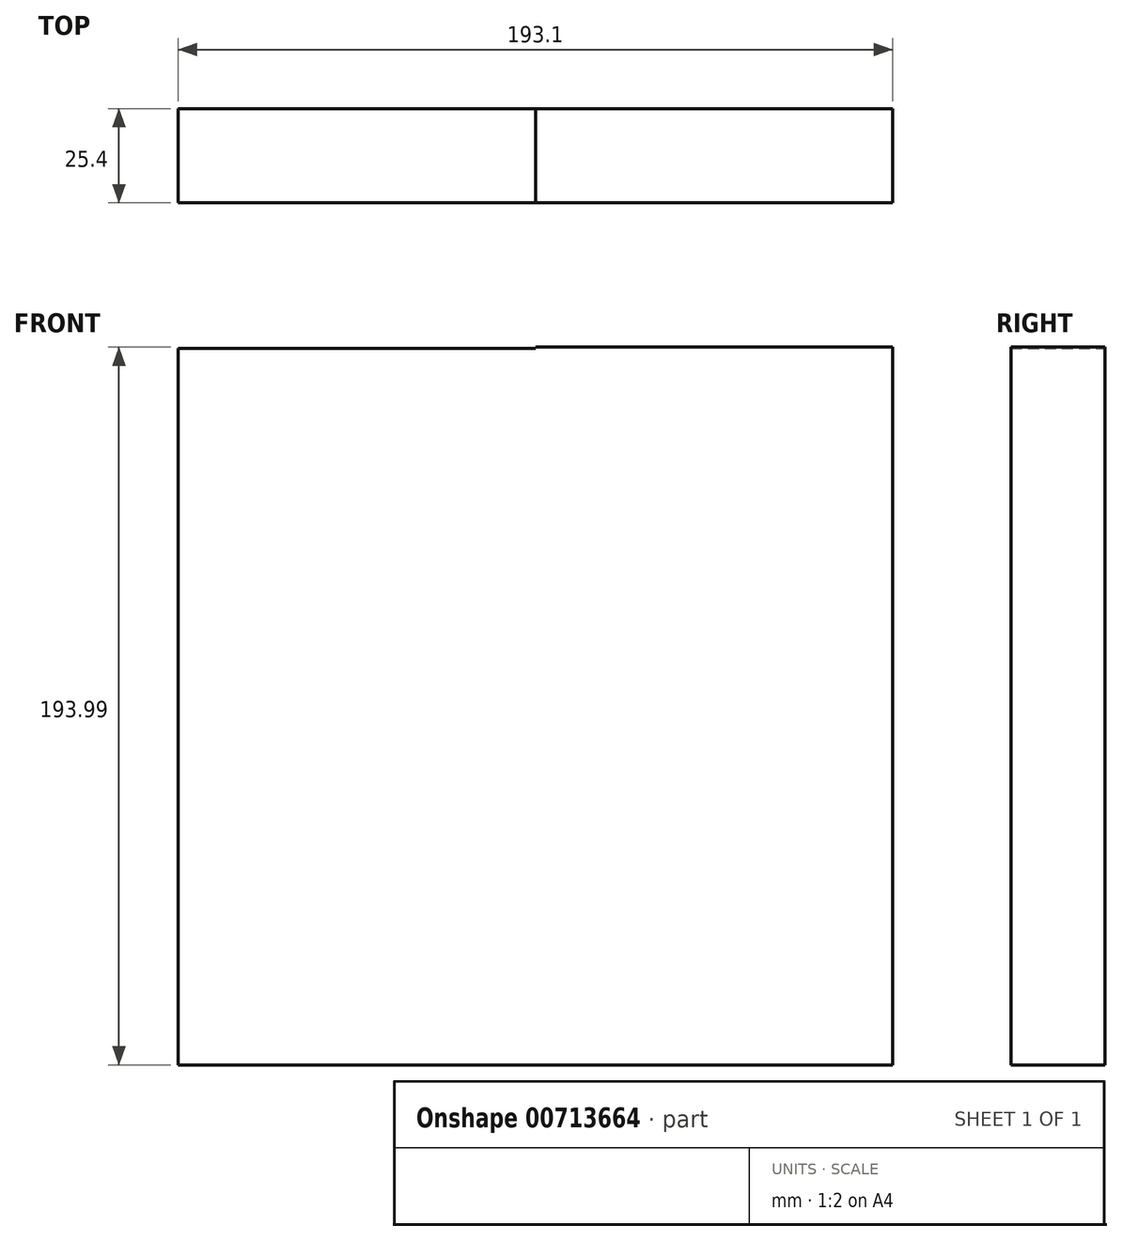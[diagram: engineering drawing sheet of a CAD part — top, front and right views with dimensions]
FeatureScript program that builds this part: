
annotation { "Feature Type Name" : "Feature", "Feature Type Description" : "" }
export const myFeature = defineFeature(function(context is Context, id is Id, definition is map)
    precondition{}
    {
        {
            var Q0;
            Q0=qCreatedBy(makeId("Front.planeOp"),FACE);
            var sketch = newSketch(context, id + "F0", { "sketchPlane" : qUnion([Q0])});
            skLineSegment(sketch, "E0.bottom", {"start": v(0, 0) * mm, "end": v(-96.6, 0) * mm});
            skLineSegment(sketch, "E0.top", {"start": v(0, 96.13) * mm, "end": v(-96.6, 96.13) * mm});
            skLineSegment(sketch, "E0.left", {"start": v(0, 0) * mm, "end": v(0, 96.13) * mm});
            skLineSegment(sketch, "E0.right", {"start": v(-96.6, 0) * mm, "end": v(-96.6, 96.13) * mm});
            skLineSegment(sketch, "E1.top", {"start": v(0, -97.48) * mm, "end": v(-96.6, -97.48) * mm});
            skLineSegment(sketch, "E1.left", {"start": v(0, 0) * mm, "end": v(0, -97.48) * mm});
            skLineSegment(sketch, "E1.right", {"start": v(-96.6, 0) * mm, "end": v(-96.6, -97.48) * mm});
            skLineSegment(sketch, "E2.bottom", {"start": v(0, -97.48) * mm, "end": v(96.49, -97.48) * mm});
            skLineSegment(sketch, "E2.top", {"start": v(0, 96.5) * mm, "end": v(96.49, 96.5) * mm});
            skLineSegment(sketch, "E2.left", {"start": v(0, -97.48) * mm, "end": v(0, 96.5) * mm});
            skLineSegment(sketch, "E2.right", {"start": v(96.49, -97.48) * mm, "end": v(96.49, 96.5) * mm});
            skLineSegment(sketch, "E3.bottom", {"start": v(0, 0) * mm, "end": v(96.49, 0) * mm});
            skLineSegment(sketch, "E3.top", {"start": v(0, -0.49) * mm, "end": v(96.49, -0.49) * mm});
            skLineSegment(sketch, "E3.left", {"start": v(0, 0) * mm, "end": v(0, -0.49) * mm});
            skLineSegment(sketch, "E3.right", {"start": v(96.49, 0) * mm, "end": v(96.49, -0.49) * mm});
            skSolve(sketch);
        }
        {
            var Q0;
            Q0 = qSketchRegion(id + "F0", true);
            extrude(context, id + "F1", {"entities" : qUnion([Q0]), "depth" : 25.4 * mm, "offsetDistance" : 25.4 * mm});
        }
    });
